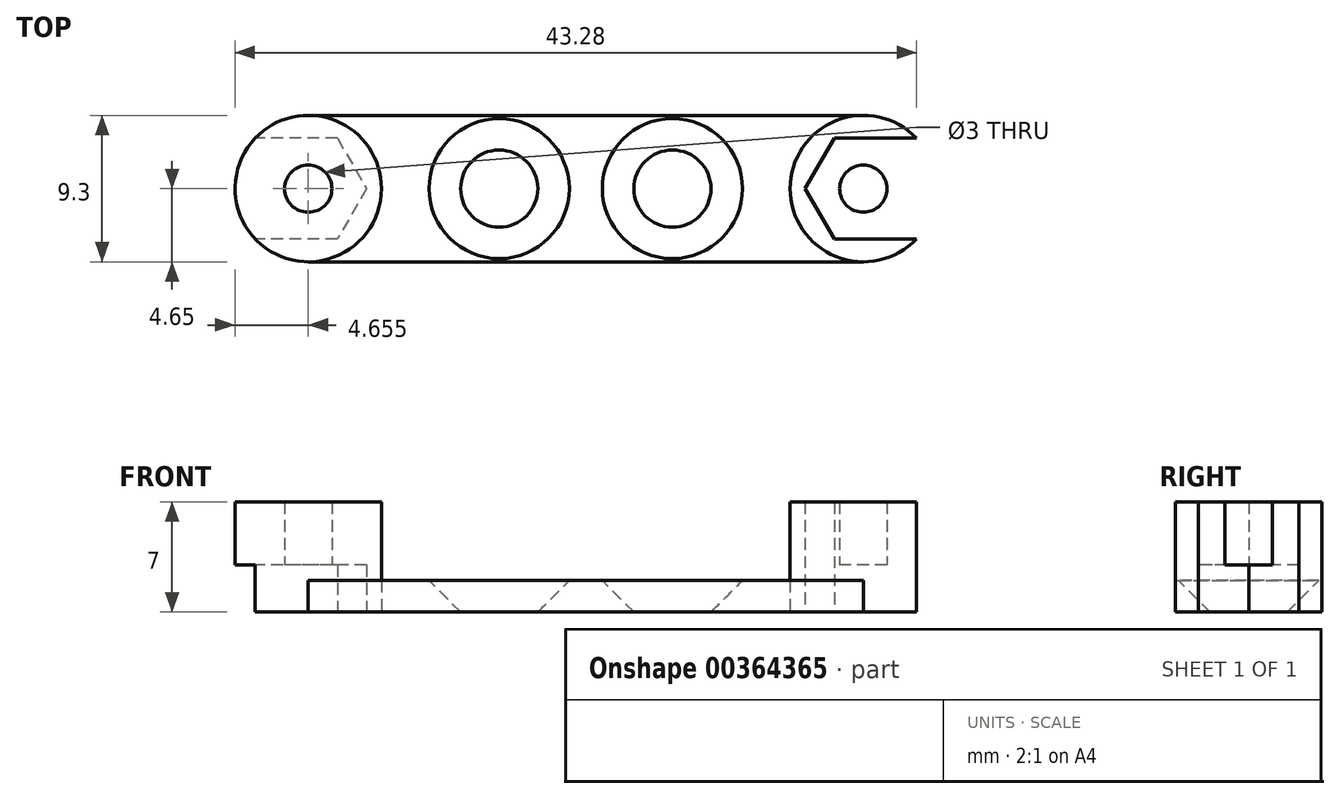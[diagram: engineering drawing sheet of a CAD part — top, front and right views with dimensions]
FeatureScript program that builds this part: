
annotation { "Feature Type Name" : "Feature", "Feature Type Description" : "" }
export const myFeature = defineFeature(function(context is Context, id is Id, definition is map)
    precondition{}
    {
        {
            var Q0;
            Q0=qCreatedBy(makeId("Top.planeOp"),FACE);
            var sketch = newSketch(context, id + "F0", { "sketchPlane" : qUnion([Q0])});
            skCircle(sketch, "E0", {"center": v(-17.62, 0) * mm, "radius": 1.5 * mm});
            skCircle(sketch, "E1", {"center": v(-17.62, 0) * mm, "radius": 4.65 * mm});
            skLineSegment(sketch, "E2", {"start": v(0, 32.14) * mm, "end": v(0, -30.96) * mm, "construction": true});
            skLineSegment(sketch, "E3", {"start": v(30.26, 0) * mm, "end": v(-35.22, 0) * mm, "construction": true});
            skPoint(sketch, "E4.middle", {"position": v(0, 0) * mm});
            skCircle(sketch, "E5", {"center": v(-5.5, 0) * mm, "radius": 2.15 * mm});
            skCircle(sketch, "E6.MirrorC", {"center": v(5.5, 0) * mm, "radius": 2.15 * mm});
            skPoint(sketch, "E7.0.midPoint", {"position": v(-17.62, 2.75) * mm});
            skCircle(sketch, "E8.MirrorC", {"center": v(17.62, 0) * mm, "radius": 4.65 * mm});
            skCircle(sketch, "E9.MirrorC", {"center": v(17.62, 0) * mm, "radius": 1.5 * mm});
            skPoint(sketch, "E10.MirrorP", {"position": v(14.87, 0) * mm});
            skLineSegment(sketch, "E11", {"start": v(-17.62, 4.65) * mm, "end": v(17.62, 4.65) * mm});
            skLineSegment(sketch, "E12", {"start": v(17.62, -4.65) * mm, "end": v(-17.62, -4.65) * mm});
            skCircle(sketch, "E13.cCircle", {"center": v(-17.62, 0) * mm, "radius": 3.2 * mm, "construction": true});
            skLineSegment(sketch, "E13.1", {"start": v(-15.78, 3.2) * mm, "end": v(-13.93, 0) * mm});
            skLineSegment(sketch, "E13.2", {"start": v(-13.93, 0) * mm, "end": v(-15.78, -3.2) * mm});
            skLineSegment(sketch, "E14", {"start": v(-15.78, -3.2) * mm, "end": v(-21, -3.2) * mm});
            skLineSegment(sketch, "E15", {"start": v(-15.78, 3.2) * mm, "end": v(-21, 3.2) * mm});
            skCircle(sketch, "E16.cCircle", {"center": v(17.63, 0) * mm, "radius": 3.2 * mm, "construction": true});
            skLineSegment(sketch, "E16.1", {"start": v(15.78, -3.2) * mm, "end": v(13.93, 0) * mm});
            skLineSegment(sketch, "E16.2", {"start": v(13.93, 0) * mm, "end": v(15.78, 3.2) * mm});
            skLineSegment(sketch, "E17", {"start": v(15.78, 3.2) * mm, "end": v(21, 3.2) * mm});
            skLineSegment(sketch, "E18", {"start": v(15.78, -3.2) * mm, "end": v(21, -3.2) * mm});
            skSolve(sketch);
        }
        {
            var Q0;
            Q0=makeQuery(id+"F0.imprint","IMPRINT",FACE,{"disambiguationData":[TD([[makeQuery(id+"F0.imprint","IMPRINT",EDGE,{"derivedFrom":sQuery(id+"F0.wireOp",EDGE,"E0")}),-1.0]])]});
            var Q1;
            Q1=makeQuery(id+"F0.imprint","IMPRINT",FACE,{"disambiguationData":[TD([[makeQuery(id+"F0.imprint","IMPRINT",EDGE,{"derivedFrom":sQuery(id+"F0.wireOp",EDGE,"fef8f7b1-8a6b-4bc8-9df2-d843bff4eec80.MirrorC")}),1.0]])]});
            var Q2;
            Q2=makeQuery(id+"F0.imprint","IMPRINT",FACE,{"disambiguationData":[TD([[makeQuery(id+"F0.imprint","IMPRINT",EDGE,{"derivedFrom":sQuery(id+"F0.wireOp",EDGE,"3c7d6f3c-1927-4e94-9eb3-e5c79b043d811.MirrorC")}),1.0]])]});
            var Q3;
            Q3=makeQuery(id+"F0.imprint","IMPRINT",FACE,{"disambiguationData":[TD([[makeQuery(id+"F0.imprint","IMPRINT",EDGE,{"derivedFrom":sQuery(id+"F0.wireOp",EDGE,"3c7d6f3c-1927-4e94-9eb3-e5c79b043d810.MirrorC")}),-1.0]])]});
            var Q4;
            Q4=makeQuery(id+"F0.imprint","IMPRINT",FACE,{"disambiguationData":[TD([[makeQuery(id+"F0.imprint","IMPRINT",EDGE,{"derivedFrom":sQuery(id+"F0.wireOp",EDGE,"E7.0")}),1.0]])]});
            var Q5;
            Q5=makeQuery(id+"F0.imprint","IMPRINT",FACE,{"disambiguationData":[TD([[makeQuery(id+"F0.imprint","IMPRINT",EDGE,{"derivedFrom":sQuery(id+"F0.wireOp",EDGE,"70040ddb-de94-4b1c-a53f-fad0beba0b010.MirrorCS")}),1.0]])]});
            var Q6;
            Q6=makeQuery(id+"F0.imprint","IMPRINT",FACE,{"disambiguationData":[TD([[makeQuery(id+"F0.imprint","IMPRINT",EDGE,{"derivedFrom":sQuery(id+"F0.wireOp",EDGE,"70040ddb-de94-4b1c-a53f-fad0beba0b010.MirrorCS")}),-1.0]])]});
            var Q7;
            Q7=makeQuery(id+"F0.imprint","IMPRINT",FACE,{"disambiguationData":[TD([[makeQuery(id+"F0.imprint","IMPRINT",EDGE,{"derivedFrom":sQuery(id+"F0.wireOp",EDGE,"70040ddb-de94-4b1c-a53f-fad0beba0b011.MirrorCS")}),-1.0]])]});
            var Q8;
            Q8=makeQuery(id+"F0.imprint","IMPRINT",FACE,{"disambiguationData":[TD([[makeQuery(id+"F0.imprint","IMPRINT",EDGE,{"derivedFrom":sQuery(id+"F0.wireOp",EDGE,"70040ddb-de94-4b1c-a53f-fad0beba0b011.MirrorCS")}),1.0]])]});
            var Q9;
            Q9=makeQuery(id+"F0.imprint","IMPRINT",FACE,{"disambiguationData":[TD([[makeQuery(id+"F0.imprint","IMPRINT",EDGE,{"derivedFrom":sQuery(id+"F0.wireOp",EDGE,"3c7d6f3c-1927-4e94-9eb3-e5c79b043d813.MirrorC")}),-1.0]])]});
            var Q10;
            Q10=makeQuery(id+"F0.imprint","IMPRINT",FACE,{"disambiguationData":[TD([[makeQuery(id+"F0.imprint","IMPRINT",EDGE,{"derivedFrom":sQuery(id+"F0.wireOp",EDGE,"3c7d6f3c-1927-4e94-9eb3-e5c79b043d812.MirrorC")}),1.0]])]});
            var Q11;
            Q11=makeQuery(id+"F0.imprint","IMPRINT",FACE,{"disambiguationData":[TD([[makeQuery(id+"F0.imprint","IMPRINT",EDGE,{"derivedFrom":sQuery(id+"F0.wireOp",EDGE,"3fe6537c-9369-4999-81a2-d7bdca3591c50.MirrorCS")}),-1.0]])]});
            var Q12;
            Q12=makeQuery(id+"F0.imprint","IMPRINT",FACE,{"disambiguationData":[TD([[makeQuery(id+"F0.imprint","IMPRINT",EDGE,{"derivedFrom":sQuery(id+"F0.wireOp",EDGE,"3fe6537c-9369-4999-81a2-d7bdca3591c50.MirrorCS")}),1.0]])]});
            var Q13;
            Q13=makeQuery(id+"F0.imprint","IMPRINT",FACE,{"disambiguationData":[TD([[makeQuery(id+"F0.imprint","IMPRINT",EDGE,{"derivedFrom":sQuery(id+"F0.wireOp",EDGE,"E13.1")}),1.0]])]});
            var Q14;
            Q14=makeQuery(id+"F0.imprint","IMPRINT",FACE,{"disambiguationData":[TD([[makeQuery(id+"F0.imprint","IMPRINT",EDGE,{"derivedFrom":sQuery(id+"F0.wireOp",EDGE,"E16.1")}),1.0]])]});
            var Q15;
            Q15=makeQuery(id+"F0.imprint","IMPRINT",FACE,{"disambiguationData":[TD([[makeQuery(id+"F0.imprint","IMPRINT",EDGE,{"derivedFrom":sQuery(id+"F0.wireOp",EDGE,"E9.MirrorC")}),1.0]])]});
            extrude(context, id + "F1", {"entities" : qUnion([Q0, Q1, Q2, Q3, Q4, Q5, Q6, Q7, Q8, Q9, Q10, Q11, Q12, Q13, Q14, Q15]), "depth" : 7 * mm});
        }
        {
            var Q0;
            {var subQ5=sQuery(id+"F0.wireOp",EDGE,"wczayVBv-H7P2-puqE-UURt-AWV69ZnfTTLc");var subQ8=sQuery(id+"F0.wireOp",EDGE,"E1");var subQ9=makeQuery(id+"F0.imprint","INTERSECT",VERTEX,{"derivedFrom":[subQ8,subQ5]});Q0=makeQuery(id+"F0.imprint","IMPRINT",FACE,{"disambiguationData":[TD([[makeQuery(id+"F0.imprint","IMPRINT",EDGE,{"disambiguationData":[TD([[subQ9,-1.0]])],"derivedFrom":subQ8}),-1.0]])]});}
            var Q1;
            {var subQ5=sQuery(id+"F0.wireOp",EDGE,"wczayVBv-H7P2-puqE-UURt-AWV69ZnfTTLc");var subQ8=sQuery(id+"F0.wireOp",EDGE,"E1");var subQ9=makeQuery(id+"F0.imprint","INTERSECT",VERTEX,{"derivedFrom":[subQ8,subQ5]});Q1=makeQuery(id+"F0.imprint","IMPRINT",FACE,{"disambiguationData":[TD([[makeQuery(id+"F0.imprint","IMPRINT",EDGE,{"disambiguationData":[TD([[subQ9,-1.0]])],"derivedFrom":subQ8}),-1.0]])]});}
            var Q2;
            {var subQ0=sQuery(id+"F0.wireOp",EDGE,"E4.right");Q2=makeQuery(id+"F0.imprint","IMPRINT",FACE,{"disambiguationData":[TD([[makeQuery(id+"F0.imprint","IMPRINT",EDGE,{"derivedFrom":subQ0}),-1.0]])]});}
            var Q3;
            {var subQ0=sQuery(id+"F0.wireOp",EDGE,"NkjpELRF-dXJl-DoJs-t607-xz73BPGU116w");var subQ1=sQuery(id+"F0.wireOp",EDGE,"3c7d6f3c-1927-4e94-9eb3-e5c79b043d810.MirrorC");var subQ2=makeQuery(id+"F0.imprint","INTERSECT",VERTEX,{"derivedFrom":[subQ1,subQ0]});Q3=makeQuery(id+"F0.imprint","IMPRINT",FACE,{"disambiguationData":[TD([[makeQuery(id+"F0.imprint","IMPRINT",EDGE,{"disambiguationData":[TD([[subQ2,-1.0]])],"derivedFrom":subQ1}),1.0]])]});}
            var Q4;
            {var subQ0=sQuery(id+"F0.wireOp",EDGE,"wmpZUQMM-aJpV-b3Hp-fgdm-3RzJsxmMfpbx");var subQ1=sQuery(id+"F0.wireOp",EDGE,"wczayVBv-H7P2-puqE-UURt-AWV69ZnfTTLc");var subQ2=makeQuery(id+"F0.imprint","INTERSECT",VERTEX,{"derivedFrom":[subQ1,subQ0]});Q4=makeQuery(id+"F0.imprint","IMPRINT",FACE,{"disambiguationData":[TD([[makeQuery(id+"F0.imprint","IMPRINT",EDGE,{"disambiguationData":[TD([[subQ2,1.0]])],"derivedFrom":subQ1}),1.0]])]});}
            var Q5;
            {var subQ0=sQuery(id+"F0.wireOp",EDGE,"NkjpELRF-dXJl-DoJs-t607-xz73BPGU116w");var subQ1=sQuery(id+"F0.wireOp",EDGE,"3c7d6f3c-1927-4e94-9eb3-e5c79b043d810.MirrorC");var subQ2=makeQuery(id+"F0.imprint","INTERSECT",VERTEX,{"derivedFrom":[subQ1,subQ0]});Q5=makeQuery(id+"F0.imprint","IMPRINT",FACE,{"disambiguationData":[TD([[makeQuery(id+"F0.imprint","IMPRINT",EDGE,{"disambiguationData":[TD([[subQ2,-1.0]])],"derivedFrom":subQ1}),1.0]])]});}
            var Q6;
            {var subQ1=sQuery(id+"F0.wireOp",EDGE,"3c7d6f3c-1927-4e94-9eb3-e5c79b043d811.MirrorC");var subQ5=sQuery(id+"F0.wireOp",EDGE,"wczayVBv-H7P2-puqE-UURt-AWV69ZnfTTLc");var subQ9=makeQuery(id+"F0.imprint","INTERSECT",VERTEX,{"derivedFrom":[subQ1,subQ5]});Q6=makeQuery(id+"F0.imprint","IMPRINT",FACE,{"disambiguationData":[TD([[makeQuery(id+"F0.imprint","IMPRINT",EDGE,{"disambiguationData":[TD([[subQ9,1.0]])],"derivedFrom":subQ1}),-1.0]])]});}
            var Q7;
            {var subQ5=sQuery(id+"F0.wireOp",EDGE,"wczayVBv-H7P2-puqE-UURt-AWV69ZnfTTLc");var subQ8=sQuery(id+"F0.wireOp",EDGE,"E1");var subQ9=makeQuery(id+"F0.imprint","INTERSECT",VERTEX,{"derivedFrom":[subQ8,subQ5]});Q7=makeQuery(id+"F0.imprint","IMPRINT",FACE,{"disambiguationData":[TD([[makeQuery(id+"F0.imprint","IMPRINT",EDGE,{"disambiguationData":[TD([[subQ9,-1.0]])],"derivedFrom":subQ8}),-1.0]])]});}
            var Q8;
            {var subQ0=sQuery(id+"F0.wireOp",EDGE,"E4.left");Q8=makeQuery(id+"F0.imprint","IMPRINT",FACE,{"disambiguationData":[TD([[makeQuery(id+"F0.imprint","IMPRINT",EDGE,{"derivedFrom":subQ0}),1.0]])]});}
            var Q9;
            {var subQ0=sQuery(id+"F0.wireOp",EDGE,"NkjpELRF-dXJl-DoJs-t607-xz73BPGU116w");var subQ1=sQuery(id+"F0.wireOp",EDGE,"3c7d6f3c-1927-4e94-9eb3-e5c79b043d810.MirrorC");var subQ2=makeQuery(id+"F0.imprint","INTERSECT",VERTEX,{"derivedFrom":[subQ1,subQ0]});Q9=makeQuery(id+"F0.imprint","IMPRINT",FACE,{"disambiguationData":[TD([[makeQuery(id+"F0.imprint","IMPRINT",EDGE,{"disambiguationData":[TD([[subQ2,-1.0]])],"derivedFrom":subQ1}),1.0]])]});}
            var Q10;
            {var subQ1=sQuery(id+"F0.wireOp",EDGE,"fef8f7b1-8a6b-4bc8-9df2-d843bff4eec81.MirrorC");var subQ4=sQuery(id+"F0.wireOp",EDGE,"NkjpELRF-dXJl-DoJs-t607-xz73BPGU116w");var subQ5=makeQuery(id+"F0.imprint","INTERSECT",VERTEX,{"derivedFrom":[subQ1,subQ4]});Q10=makeQuery(id+"F0.imprint","IMPRINT",FACE,{"disambiguationData":[TD([[makeQuery(id+"F0.imprint","IMPRINT",EDGE,{"disambiguationData":[TD([[subQ5,1.0]])],"derivedFrom":subQ1}),1.0]])]});}
            extrude(context, id + "F2", {"entities" : qUnion([Q0, Q1, Q2, Q3, Q4, Q5, Q6, Q7, Q8, Q9, Q10]), "depth" : 2 * mm});
        }
        {
            var Q0;
            Q0=makeQuery(id+"F2.opExtrude","CAP_EDGE",EDGE,{"disambiguationData":[OSD([sQuery(id+"F0.wireOp",EDGE,"E5")])],"isStart":false});
            var Q1;
            Q1=makeQuery(id+"F2.opExtrude","CAP_EDGE",EDGE,{"disambiguationData":[OSD([sQuery(id+"F0.wireOp",EDGE,"E6.MirrorC")])],"isStart":false});
            chamfer(context, id + "F3", {"entities" : qUnion([Q0, Q1]), "width" : 2.3 * mm, "tangentPropagation" : true});
        }
        {
            var Q0;
            Q0=makeQuery(id+"F0.imprint","IMPRINT",FACE,{"disambiguationData":[TD([[makeQuery(id+"F0.imprint","IMPRINT",EDGE,{"derivedFrom":sQuery(id+"F0.wireOp",EDGE,"E0")}),-1.0]])]});
            var Q1;
            Q1=makeQuery(id+"F0.imprint","IMPRINT",FACE,{"disambiguationData":[TD([[makeQuery(id+"F0.imprint","IMPRINT",EDGE,{"derivedFrom":sQuery(id+"F0.wireOp",EDGE,"3fe6537c-9369-4999-81a2-d7bdca3591c50.MirrorCS")}),1.0]])]});
            var Q2;
            Q2=makeQuery(id+"F0.imprint","IMPRINT",FACE,{"disambiguationData":[TD([[makeQuery(id+"F0.imprint","IMPRINT",EDGE,{"derivedFrom":sQuery(id+"F0.wireOp",EDGE,"E9.MirrorC")}),1.0]])]});
            extrude(context, id + "F4", {"entities" : qUnion([Q0, Q1, Q2]), "operationType" : NewBodyOperationType.REMOVE, "depth" : 3 * mm});
        }
    });
